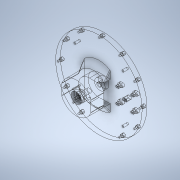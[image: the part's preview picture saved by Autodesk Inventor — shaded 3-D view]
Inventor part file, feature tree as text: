
AUTODESK INVENTOR PART (.ipt)
format: ipt  version: 2020.3 (Build 243373000, 373)  size: 467,456 bytes
history: native  units: mm
features: extrude x18, sketch x18, pattern_circular x3, pattern_linear x1, chamfer x1, fillet x1
ambient origin geometry x8: Origin, YZ Plane, XZ Plane, XY Plane, X Axis, Y Axis, Z Axis, Center Point
bodies: Solid1 (feature_tree)
feature tree (42):
  extrude  "Extrusion1"  Depth=22.0mm
  extrude  "Extrusion2"  Depth=8.6mm
  extrude  "Extrusion3"  Depth=2.0mm
  extrude  "Extrusion4"  Depth=10.0mm TaperAngle=0.0deg
  extrude  "Extrusion5"  Depth=10.0mm
  extrude  "Extrusion6"  Depth=22.0mm
  extrude  "Extrusion7"  Depth=47.0mm TaperAngle=0.0deg
  extrude  "Extrusion11"  Depth=14.0mm
  pattern_circular  "Circular Pattern1"  Count=3 Angle=360.0deg
  extrude  "Extrusion14"  Depth=7.2mm TaperAngle=0.0deg
  extrude  "Extrusion18"  Depth=3.2mm
  extrude  "Extrusion19"  Depth=10.0mm TaperAngle=0.0deg
  pattern_circular  "Circular Pattern3"  Count=11 Angle=300.0deg
  extrude  "Extrusion20"  Depth=2.7mm
  extrude  "Extrusion21"  Depth=54.0mm
  extrude  "Extrusion22"  Depth=4.0mm
  extrude  "Extrusion23"  Depth=15.5mm
  pattern_circular  "Circular Pattern4"  [2 undecoded]
  extrude  "Extrusion24"  Depth=2.0mm
  pattern_linear  "Rectangular Pattern2"  Spacing1=4.0mm  [1 undecoded]
  chamfer  "Chamfer2"  Angle=120.0deg  [1 undecoded]
  extrude  "Extrusion25"  TaperAngle=120.0deg  [1 undecoded]
  extrude  "Extrusion27"  Depth=2.0mm
  fillet  "Fillet4"  Radius=4.0mm
  sketch  "Sketch1"  dims[d0=180.0mm d1=22.0mm]
  sketch  "Sketch3"  dims[d2=8.0mm d3=0.0mm d4=8.6mm]
  sketch  "Sketch4"  dims[d5=2.0mm d6=0.0mm d7=45.0mm]
  sketch  "Sketch5"  dims[d8=10.0mm d9=20.0mm d10=0.0mm]
  sketch  "Sketch6"  dims[d13=10.0mm d14=0.0mm d15=8.6mm]
  sketch  "Sketch7"  dims[d16=20.0mm d17=0.0mm d18=22.0mm]
  sketch  "Sketch8"  dims[d19=7.0mm d20=0.0mm d23=47.0mm d24=0.0mm]
  sketch  "Sketch12"  dims[d43=2.5mm d44=14.0mm]
  sketch  "Sketch17"  dims[d45=15.0mm d46=0.0mm d47=30.0mm d48=360.0deg]
  sketch  "Sketch21"  dims[d62=15.0mm d63=7.2mm d64=0.0mm]
  sketch  "Sketch22"  dims[d87=85.0mm d88=3.2mm]
  sketch  "Sketch23"  dims[d89=10.0mm d90=0.0mm d92=5.0mm d93=0.0mm d94=110.0mm d95=300.0deg]
  sketch  "Sketch24"  dims[d97=210.0deg d98=2.7mm]
  sketch  "Sketch26"  dims[d99=4.0mm d100=54.0mm]
  sketch  "Sketch27"  dims[d105=1.6mm d107=4.0mm]
  sketch  "Sketch28"  dims[d108=15.5mm d109=15.5mm]
  sketch  "Sketch29"  dims[d110=10.0mm d111=0.0mm]
  sketch  "Sketch31"  dims[d112=21.5mm d113=10.0mm d114=0.0mm d115=3.5mm d116=4.0mm d117=0.0mm d124=120.0deg d125=120.0deg d126=5.7mm d127=4.0mm d128=50.0mm d129=50.0mm d130=10.0mm d131=0.0mm d132=40.0mm d133=360.0deg d135=10.0mm d136=0.0mm d137=20.0mm d139=31.0mm d140=20.0mm d142=31.0mm d143=0.174533mm d144=0.349066mm d145=12.0mm d146=2.0mm d147=45.0deg d148=20.0mm d149=40.0mm d150=40.0mm d151=15.0mm d152=0.0mm d161=40.0mm d162=40.0mm d163=20.0mm d164=30.0mm d165=0.0mm d166=2.0mm]
note: 5 required parameter values undecoded (feature->parameter linkage not recoverable at this tier; creation-order binding heuristic only, values carry confidence <= 0.55)
